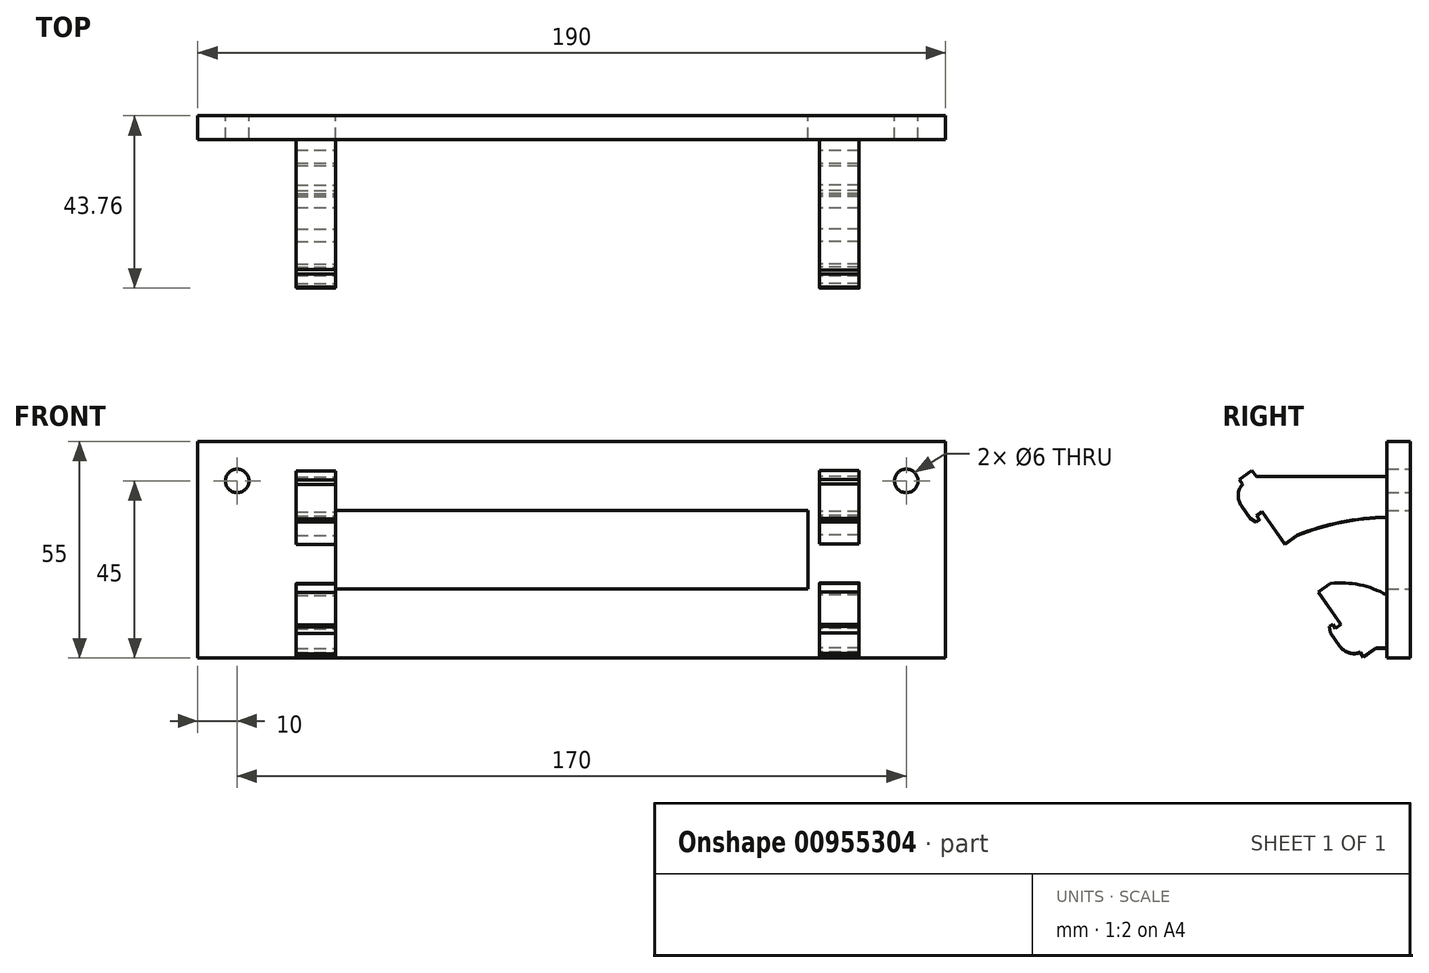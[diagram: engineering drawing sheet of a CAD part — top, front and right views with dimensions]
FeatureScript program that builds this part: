
annotation { "Feature Type Name" : "Feature", "Feature Type Description" : "" }
export const myFeature = defineFeature(function(context is Context, id is Id, definition is map)
    precondition{}
    {
        {
            var Q0;
            Q0=qCreatedBy(makeId("Front.planeOp"),FACE);
            var sketch = newSketch(context, id + "F0", { "sketchPlane" : qUnion([Q0])});
            skLineSegment(sketch, "E0.bottom", {"start": v(0, 0) * mm, "end": v(150, 0) * mm});
            skLineSegment(sketch, "E0.top", {"start": v(0, 35) * mm, "end": v(150, 35) * mm});
            skLineSegment(sketch, "E0.left", {"start": v(0, 0) * mm, "end": v(0, 35) * mm});
            skLineSegment(sketch, "E0.right", {"start": v(150, 0) * mm, "end": v(150, 35) * mm});
            skSolve(sketch);
        }
        {
            var Q0;
            Q0=qCreatedBy(makeId("Front.planeOp"),FACE);
            var sketch = newSketch(context, id + "F1", { "sketchPlane" : qUnion([Q0])});
            skLineSegment(sketch, "E1.bottom", {"start": v(15, 7.5) * mm, "end": v(135, 7.5) * mm});
            skLineSegment(sketch, "E1.top", {"start": v(15, 27.5) * mm, "end": v(135, 27.5) * mm});
            skLineSegment(sketch, "E1.left", {"start": v(15, 7.5) * mm, "end": v(15, 27.5) * mm});
            skLineSegment(sketch, "E1.right", {"start": v(135, 7.5) * mm, "end": v(135, 27.5) * mm});
            skLineSegment(sketch, "E2.bottom", {"start": v(-20, -10) * mm, "end": v(170, -10) * mm});
            skLineSegment(sketch, "E2.top", {"start": v(-20, 45) * mm, "end": v(170, 45) * mm});
            skLineSegment(sketch, "E2.left", {"start": v(-20, -10) * mm, "end": v(-20, 45) * mm});
            skLineSegment(sketch, "E2.right", {"start": v(170, -10) * mm, "end": v(170, 45) * mm});
            skCircle(sketch, "E3", {"center": v(-10, 35) * mm, "radius": 3 * mm});
            skCircle(sketch, "E4", {"center": v(160, 35) * mm, "radius": 3 * mm});
            skSolve(sketch);
        }
        {
            var Q0;
            Q0 = qSketchRegion(id + "F1", true);
            extrude(context, id + "F2", {"entities" : qUnion([Q0]), "depth" : 6 * mm, "offsetDistance" : 25 * mm});
        }
        {
            var Q0;
            Q0=qCreatedBy(makeId("Right.planeOp"),FACE);
            cPlane(context, id + "F3", {"entities" : qUnion([Q0]), "cplaneType" : CPlaneType.OFFSET, "offset" : 138 * mm, "width" : 150 * mm, "height" : 150 * mm});
        }
        {
            var Q0;
            Q0=qCreatedBy(makeId("Right.planeOp"),FACE);
            cPlane(context, id + "F4", {"entities" : qUnion([Q0]), "cplaneType" : CPlaneType.OFFSET, "offset" : 10 * mm, "width" : 150 * mm, "height" : 150 * mm});
        }
        {
            var Q0;
            Q0=qCreatedBy(id+"F3.planeOp",FACE);
            var sketch = newSketch(context, id + "F5", { "sketchPlane" : qUnion([Q0])});
            skLineSegment(sketch, "E5.bottom", {"start": v(-37.71, 27.19) * mm, "end": v(-38.94, 26.33) * mm});
            skLineSegment(sketch, "E5.top", {"start": v(-17.64, -1.48) * mm, "end": v(-18.87, -2.34) * mm});
            skLineSegment(sketch, "E6.left", {"start": v(12.34, 21.42) * mm, "end": v(12.34, 21.42) * mm});
            skLineSegment(sketch, "E7", {"start": v(-37.71, 27.19) * mm, "end": v(-39.12, 26.2) * mm});
            skLineSegment(sketch, "E8", {"start": v(-39.12, 26.2) * mm, "end": v(-38.42, 25.2) * mm});
            skLineSegment(sketch, "E9", {"start": v(-38.42, 25.2) * mm, "end": v(-39.24, 24.62) * mm});
            skLineSegment(sketch, "E10", {"start": v(-39.24, 24.62) * mm, "end": v(-40.67, 25.43) * mm});
            skLineSegment(sketch, "E11", {"start": v(-40.67, 25.43) * mm, "end": v(-42.96, 28.7) * mm});
            skArc(sketch, "E12", {"start": v(-42.64, 34.19) * mm, "mid": v(-43.75, 31.5) * mm, "end": v(-42.96, 28.7) * mm});
            skLineSegment(sketch, "E13", {"start": v(-22.61, 17.72) * mm, "end": v(-6.75, 17.72) * mm});
            skArc(sketch, "E14.MirrorCS", {"start": v(-12.74, -8.5) * mm, "mid": v(-15.65, -8.64) * mm, "end": v(-18, -6.94) * mm});
            skLineSegment(sketch, "E15.MirrorCS", {"start": v(-20.3, -3.66) * mm, "end": v(-18, -6.94) * mm});
            skLineSegment(sketch, "E16.MirrorCS", {"start": v(-20.57, -2.04) * mm, "end": v(-20.3, -3.66) * mm});
            skLineSegment(sketch, "E17.MirrorCS", {"start": v(-19.76, -1.46) * mm, "end": v(-20.57, -2.04) * mm});
            skLineSegment(sketch, "E18.MirrorCS", {"start": v(-17.64, -1.48) * mm, "end": v(-19.05, -2.47) * mm});
            skLineSegment(sketch, "E19.MirrorCS", {"start": v(-19.05, -2.47) * mm, "end": v(-19.76, -1.46) * mm});
            skLineSegment(sketch, "E20", {"start": v(-17.64, -1.48) * mm, "end": v(-12.74, -8.5) * mm});
            skLineSegment(sketch, "E21.bottom", {"start": v(-43.52, 35.33) * mm, "end": v(-40.24, 37.63) * mm});
            skLineSegment(sketch, "E21.right", {"start": v(-40.24, 37.63) * mm, "end": v(-28.77, 21.24) * mm});
            skLineSegment(sketch, "E22.bottom", {"start": v(-12.08, -9.7) * mm, "end": v(-8.8, -7.4) * mm});
            skLineSegment(sketch, "E22.right", {"start": v(-8.8, -7.4) * mm, "end": v(-20.28, 8.98) * mm});
            skLineSegment(sketch, "E23", {"start": v(-40.1, 36.06) * mm, "end": v(-4.43, 36.06) * mm});
            skLineSegment(sketch, "E24", {"start": v(-4.43, 36.06) * mm, "end": v(-4.43, 25.82) * mm});
            skArc(sketch, "E25", {"start": v(-4.43, 25.82) * mm, "mid": v(-16.81, 24.68) * mm, "end": v(-28.77, 21.24) * mm});
            skLineSegment(sketch, "E26", {"start": v(-8.8, -7.4) * mm, "end": v(-4.13, -7.4) * mm});
            skLineSegment(sketch, "E27", {"start": v(-4.13, -7.4) * mm, "end": v(-4.13, 4.85) * mm});
            skArc(sketch, "E28", {"start": v(-4.13, 4.85) * mm, "mid": v(-11.84, 8.33) * mm, "end": v(-20.28, 8.98) * mm});
            skLineSegment(sketch, "E29", {"start": v(-17.64, -1.48) * mm, "end": v(-23.42, 6.78) * mm});
            skLineSegment(sketch, "E30", {"start": v(-23.42, 6.78) * mm, "end": v(-20.28, 8.98) * mm});
            skLineSegment(sketch, "E31", {"start": v(-12.74, -8.5) * mm, "end": v(-12.08, -9.7) * mm});
            skLineSegment(sketch, "E32", {"start": v(-37.71, 27.19) * mm, "end": v(-31.96, 19.01) * mm});
            skLineSegment(sketch, "E33", {"start": v(-31.96, 19.01) * mm, "end": v(-28.77, 21.24) * mm});
            skLineSegment(sketch, "E34", {"start": v(-43.52, 35.33) * mm, "end": v(-42.64, 34.19) * mm});
            skSolve(sketch);
        }
        {
            var Q0;
            Q0=qCreatedBy(id+"F4.planeOp",FACE);
            var sketch = newSketch(context, id + "F6", { "sketchPlane" : qUnion([Q0])});
            skLineSegment(sketch, "E35.bottom", {"start": v(-37.66, 27.09) * mm, "end": v(-38.89, 26.23) * mm});
            skLineSegment(sketch, "E35.top", {"start": v(-17.58, -1.58) * mm, "end": v(-18.81, -2.44) * mm});
            skLineSegment(sketch, "E36.left", {"start": v(12.34, 21.42) * mm, "end": v(12.34, 21.42) * mm});
            skLineSegment(sketch, "E37", {"start": v(-37.66, 27.09) * mm, "end": v(-39.07, 26.1) * mm});
            skLineSegment(sketch, "E38", {"start": v(-39.07, 26.1) * mm, "end": v(-38.36, 25.1) * mm});
            skLineSegment(sketch, "E39", {"start": v(-38.36, 25.1) * mm, "end": v(-39.18, 24.52) * mm});
            skLineSegment(sketch, "E40", {"start": v(-39.18, 24.52) * mm, "end": v(-40.61, 25.33) * mm});
            skLineSegment(sketch, "E41", {"start": v(-40.61, 25.33) * mm, "end": v(-42.9, 28.6) * mm});
            skArc(sketch, "E42", {"start": v(-42.58, 34.09) * mm, "mid": v(-43.7, 31.4) * mm, "end": v(-42.9, 28.6) * mm});
            skLineSegment(sketch, "E43", {"start": v(-22.56, 17.62) * mm, "end": v(-6.7, 17.62) * mm});
            skArc(sketch, "E44.MirrorCS", {"start": v(-12.69, -8.6) * mm, "mid": v(-15.6, -8.74) * mm, "end": v(-17.95, -7.04) * mm});
            skLineSegment(sketch, "E45.MirrorCS", {"start": v(-20.24, -3.76) * mm, "end": v(-17.95, -7.04) * mm});
            skLineSegment(sketch, "E46.MirrorCS", {"start": v(-20.52, -2.14) * mm, "end": v(-20.24, -3.76) * mm});
            skLineSegment(sketch, "E47.MirrorCS", {"start": v(-19.7, -1.56) * mm, "end": v(-20.52, -2.14) * mm});
            skLineSegment(sketch, "E48.MirrorCS", {"start": v(-17.58, -1.58) * mm, "end": v(-19, -2.57) * mm});
            skLineSegment(sketch, "E49.MirrorCS", {"start": v(-19, -2.57) * mm, "end": v(-19.7, -1.56) * mm});
            skLineSegment(sketch, "E50", {"start": v(-17.58, -1.58) * mm, "end": v(-12.69, -8.6) * mm});
            skLineSegment(sketch, "E51.bottom", {"start": v(-43.46, 35.23) * mm, "end": v(-40.18, 37.53) * mm});
            skLineSegment(sketch, "E51.right", {"start": v(-40.18, 37.53) * mm, "end": v(-28.71, 21.14) * mm});
            skLineSegment(sketch, "E52.bottom", {"start": v(-12.03, -9.8) * mm, "end": v(-8.75, -7.5) * mm});
            skLineSegment(sketch, "E52.right", {"start": v(-8.75, -7.5) * mm, "end": v(-20.22, 8.88) * mm});
            skLineSegment(sketch, "E53", {"start": v(-40.04, 35.96) * mm, "end": v(-4.37, 35.96) * mm});
            skLineSegment(sketch, "E54", {"start": v(-4.37, 35.96) * mm, "end": v(-4.37, 25.72) * mm});
            skArc(sketch, "E55", {"start": v(-4.37, 25.72) * mm, "mid": v(-16.76, 24.58) * mm, "end": v(-28.71, 21.14) * mm});
            skLineSegment(sketch, "E56", {"start": v(-8.75, -7.5) * mm, "end": v(-4.07, -7.5) * mm});
            skLineSegment(sketch, "E57", {"start": v(-4.07, -7.5) * mm, "end": v(-4.07, 4.75) * mm});
            skArc(sketch, "E58", {"start": v(-4.07, 4.75) * mm, "mid": v(-11.78, 8.23) * mm, "end": v(-20.22, 8.88) * mm});
            skLineSegment(sketch, "E59", {"start": v(-31.92, 18.9) * mm, "end": v(-28.71, 21.14) * mm});
            skLineSegment(sketch, "E60", {"start": v(-20.22, 8.88) * mm, "end": v(-23.36, 6.68) * mm});
            skLineSegment(sketch, "E61", {"start": v(-12.69, -8.6) * mm, "end": v(-12.03, -9.8) * mm});
            skLineSegment(sketch, "E62", {"start": v(-23.36, 6.68) * mm, "end": v(-17.58, -1.58) * mm});
            skLineSegment(sketch, "E63", {"start": v(-43.46, 35.23) * mm, "end": v(-42.58, 34.09) * mm});
            skLineSegment(sketch, "E64", {"start": v(-37.66, 27.09) * mm, "end": v(-31.92, 18.9) * mm});
            skSolve(sketch);
        }
        {
            var Q0;
            Q0 = qSketchRegion(id + "F6", true);
            extrude(context, id + "F7", {"entities" : qUnion([Q0]), "operationType" : NewBodyOperationType.ADD, "endBound" : BoundingType.SYMMETRIC, "oppositeDirection" : true, "depth" : 10 * mm, "offsetDistance" : 25 * mm});
        }
        {
            var Q0;
            Q0 = qSketchRegion(id + "F5", true);
            extrude(context, id + "F8", {"entities" : qUnion([Q0]), "operationType" : NewBodyOperationType.ADD, "depth" : 10 * mm, "offsetDistance" : 25 * mm});
        }
    });
